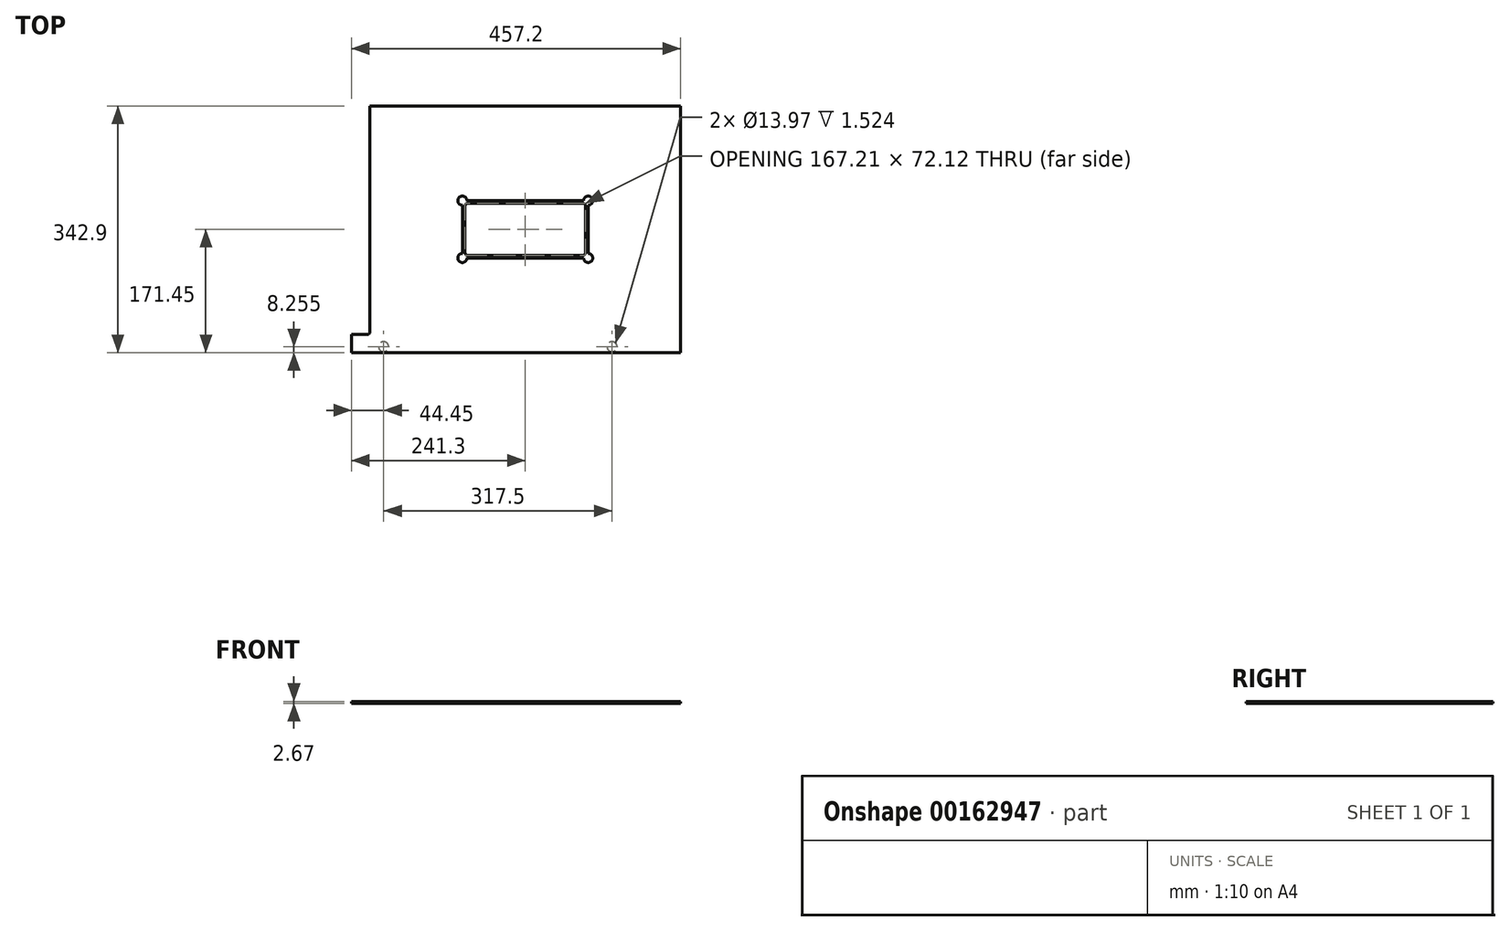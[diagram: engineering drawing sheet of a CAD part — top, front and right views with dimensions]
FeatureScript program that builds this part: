
annotation { "Feature Type Name" : "Feature", "Feature Type Description" : "" }
export const myFeature = defineFeature(function(context is Context, id is Id, definition is map)
    precondition{}
    {
        {
            var Q0;
            Q0=qCreatedBy(makeId("Top.planeOp"),FACE);
            var sketch = newSketch(context, id + "F0", { "sketchPlane" : qUnion([Q0])});
            skLineSegment(sketch, "E0.bottom", {"start": v(-215.9, 171.45) * mm, "end": v(215.9, 171.45) * mm});
            skLineSegment(sketch, "E0.left", {"start": v(-215.9, 171.45) * mm, "end": v(-215.9, -142.88) * mm});
            skLineSegment(sketch, "E0.right", {"start": v(215.9, 171.45) * mm, "end": v(215.9, -171.45) * mm});
            skPoint(sketch, "E0.middle", {"position": v(0, 0) * mm});
            skLineSegment(sketch, "E1.top", {"start": v(-219.08, -146.05) * mm, "end": v(-241.3, -146.05) * mm});
            skLineSegment(sketch, "E1.right", {"start": v(-241.3, -171.45) * mm, "end": v(-241.3, -146.05) * mm});
            skLineSegment(sketch, "E2", {"start": v(-241.3, -171.45) * mm, "end": v(215.9, -171.45) * mm});
            skLineSegment(sketch, "E3", {"start": v(-215.9, 171.45) * mm, "end": v(215.9, -171.45) * mm, "construction": true});
            skPoint(sketch, "E4.visualSharp", {"position": v(-215.9, -146.05) * mm});
            skArc(sketch, "E4.filletArc", {"start": v(-219.08, -146.05) * mm, "mid": v(-216.83, -145.12) * mm, "end": v(-215.9, -142.88) * mm});
            skSolve(sketch);
        }
        {
            var Q0;
            Q0 = qSketchRegion(id + "F0", true);
            extrude(context, id + "F1", {"entities" : qUnion([Q0]), "depth" : 2.67 * mm});
        }
        {
            var Q0;
            Q0=makeQuery(id+"F1.opExtrude","CAP_FACE",FACE,{"disambiguationData":[OSD([sQuery(id+"F0.wireOp",EDGE,"E0.bottom"),sQuery(id+"F0.wireOp",EDGE,"E0.left"),sQuery(id+"F0.wireOp",EDGE,"E0.right"),sQuery(id+"F0.wireOp",EDGE,"E1.top"),sQuery(id+"F0.wireOp",EDGE,"E1.right"),sQuery(id+"F0.wireOp",EDGE,"E2"),sQuery(id+"F0.wireOp",EDGE,"E4.filletArc")])],"isStart":true});
            var sketch = newSketch(context, id + "F2", { "sketchPlane" : qUnion([Q0])});
            skLineSegment(sketch, "E5", {"start": v(-241.3, 163.2) * mm, "end": v(215.9, 163.2) * mm, "construction": true});
            skCircle(sketch, "E6", {"center": v(-196.85, 163.2) * mm, "radius": 6.99 * mm});
            skCircle(sketch, "E7", {"center": v(120.65, 163.2) * mm, "radius": 6.99 * mm});
            skSolve(sketch);
        }
        {
            var Q0;
            Q0 = qSketchRegion(id + "F2", true);
            extrude(context, id + "F3", {"entities" : qUnion([Q0]), "operationType" : NewBodyOperationType.REMOVE, "oppositeDirection" : true, "depth" : 1.52 * mm});
        }
        {
            var Q0;
            Q0=makeQuery(id+"F1.opExtrude","CAP_FACE",FACE,{"disambiguationData":[OSD([sQuery(id+"F0.wireOp",EDGE,"E0.bottom"),sQuery(id+"F0.wireOp",EDGE,"E0.left"),sQuery(id+"F0.wireOp",EDGE,"E0.right"),sQuery(id+"F0.wireOp",EDGE,"E1.top"),sQuery(id+"F0.wireOp",EDGE,"E1.right"),sQuery(id+"F0.wireOp",EDGE,"E2"),sQuery(id+"F0.wireOp",EDGE,"E4.filletArc")])],"isStart":false});
            var sketch = newSketch(context, id + "F4", { "sketchPlane" : qUnion([Q0])});
            skLineSegment(sketch, "E8.bottom", {"start": v(86.92, -39.37) * mm, "end": v(-86.92, -39.37) * mm, "construction": true});
            skLineSegment(sketch, "E8.top", {"start": v(86.92, 39.37) * mm, "end": v(-86.92, 39.37) * mm, "construction": true});
            skLineSegment(sketch, "E8.left", {"start": v(86.92, -39.37) * mm, "end": v(86.92, 39.37) * mm, "construction": true});
            skLineSegment(sketch, "E8.right", {"start": v(-86.92, -39.37) * mm, "end": v(-86.92, 39.37) * mm, "construction": true});
            skPoint(sketch, "E8.middle", {"position": v(0, 0) * mm});
            skLineSegment(sketch, "E9.0", {"start": v(81.07, -39.87) * mm, "end": v(-81.07, -39.87) * mm});
            skLineSegment(sketch, "E9.1", {"start": v(87.42, -33.52) * mm, "end": v(87.42, 33.52) * mm});
            skLineSegment(sketch, "E9.2", {"start": v(81.07, 39.87) * mm, "end": v(-81.07, 39.87) * mm});
            skLineSegment(sketch, "E9.3", {"start": v(-87.42, -33.52) * mm, "end": v(-87.42, 33.52) * mm});
            skLineSegment(sketch, "E10.0", {"start": v(80.43, 36.06) * mm, "end": v(-80.43, 36.06) * mm});
            skLineSegment(sketch, "E10.1", {"start": v(83.6, -32.89) * mm, "end": v(83.6, 32.88) * mm});
            skLineSegment(sketch, "E10.2", {"start": v(80.43, -36.06) * mm, "end": v(-80.43, -36.06) * mm});
            skLineSegment(sketch, "E10.3", {"start": v(-83.6, -32.88) * mm, "end": v(-83.6, 32.89) * mm});
            skPoint(sketch, "E11.visualSharp", {"position": v(-83.6, 36.06) * mm});
            skArc(sketch, "E11.filletArc", {"start": v(-80.43, 36.06) * mm, "mid": v(-82.68, 35.13) * mm, "end": v(-83.6, 32.89) * mm});
            skPoint(sketch, "E12.visualSharp", {"position": v(83.6, 36.06) * mm});
            skArc(sketch, "E12.filletArc", {"start": v(83.6, 32.88) * mm, "mid": v(82.68, 35.13) * mm, "end": v(80.43, 36.06) * mm});
            skPoint(sketch, "E13.visualSharp", {"position": v(-83.6, -36.06) * mm});
            skArc(sketch, "E13.filletArc", {"start": v(-83.6, -32.88) * mm, "mid": v(-82.68, -35.13) * mm, "end": v(-80.43, -36.06) * mm});
            skPoint(sketch, "E14.visualSharp", {"position": v(83.6, -36.06) * mm});
            skArc(sketch, "E14.filletArc", {"start": v(80.43, -36.06) * mm, "mid": v(82.68, -35.13) * mm, "end": v(83.6, -32.88) * mm});
            skArc(sketch, "E15", {"start": v(-81.07, 39.87) * mm, "mid": v(-91.9, 44.36) * mm, "end": v(-87.42, 33.52) * mm});
            skArc(sketch, "E16", {"start": v(87.42, 33.52) * mm, "mid": v(91.9, 44.36) * mm, "end": v(81.07, 39.87) * mm});
            skArc(sketch, "E17", {"start": v(81.07, -39.87) * mm, "mid": v(91.9, -44.36) * mm, "end": v(87.42, -33.52) * mm});
            skArc(sketch, "E18", {"start": v(-87.42, -33.52) * mm, "mid": v(-91.9, -44.36) * mm, "end": v(-81.07, -39.87) * mm});
            skSolve(sketch);
        }
        {
            var Q0;
            Q0 = qSketchRegion(id + "F4", true);
            extrude(context, id + "F5", {"entities" : qUnion([Q0]), "operationType" : NewBodyOperationType.REMOVE, "oppositeDirection" : true, "depth" : 0.83 * mm});
        }
        {
            var Q0;
            {var subQ0=sQuery(id+"F0.wireOp",EDGE,"E4.filletArc");var subQ1=sQuery(id+"F0.wireOp",EDGE,"E2");var subQ2=sQuery(id+"F0.wireOp",EDGE,"E1.right");var subQ3=sQuery(id+"F0.wireOp",EDGE,"E0.bottom");var subQ4=sQuery(id+"F0.wireOp",EDGE,"E0.left");var subQ5=sQuery(id+"F0.wireOp",EDGE,"E0.right");var subQ6=sQuery(id+"F0.wireOp",EDGE,"E1.top");Q0=makeQuery(id+"F5.boolean.opBoolean","SPLIT",FACE,{"disambiguationData":[TD([makeQuery(id+"F1.opExtrude","SWEPT_FACE",FACE,{"disambiguationData":[OSD([subQ3])]})])],"derivedFrom":makeQuery(id+"F1.opExtrude","CAP_FACE",FACE,{"disambiguationData":[OSD([subQ3,subQ4,subQ5,subQ6,subQ2,subQ1,subQ0])],"isStart":false})});}
            var sketch = newSketch(context, id + "F6", { "sketchPlane" : qUnion([Q0])});
            skArc(sketch, "E19.0.0", {"start": v(83.6, 32.88) * mm, "mid": v(82.68, 35.13) * mm, "end": v(80.43, 36.06) * mm});
            skLineSegment(sketch, "E19.0.1", {"start": v(80.43, 36.06) * mm, "end": v(-80.43, 36.06) * mm});
            skArc(sketch, "E19.0.2", {"start": v(-80.43, 36.06) * mm, "mid": v(-82.68, 35.13) * mm, "end": v(-83.6, 32.89) * mm});
            skLineSegment(sketch, "E19.0.3", {"start": v(-83.6, 32.89) * mm, "end": v(-83.6, -32.88) * mm});
            skArc(sketch, "E19.0.4", {"start": v(-83.6, -32.88) * mm, "mid": v(-82.68, -35.13) * mm, "end": v(-80.43, -36.06) * mm});
            skLineSegment(sketch, "E19.0.5", {"start": v(-80.43, -36.06) * mm, "end": v(80.43, -36.06) * mm});
            skArc(sketch, "E19.0.6", {"start": v(80.43, -36.06) * mm, "mid": v(82.68, -35.13) * mm, "end": v(83.6, -32.88) * mm});
            skLineSegment(sketch, "E19.0.7", {"start": v(83.6, -32.89) * mm, "end": v(83.6, 32.88) * mm});
            skSolve(sketch);
        }
        {
            var Q0;
            Q0 = qSketchRegion(id + "F6", true);
            extrude(context, id + "F7", {"entities" : qUnion([Q0]), "operationType" : NewBodyOperationType.REMOVE, "endBound" : BoundingType.THROUGH_ALL, "oppositeDirection" : true, "depth" : 25.4 * mm});
        }
    });
